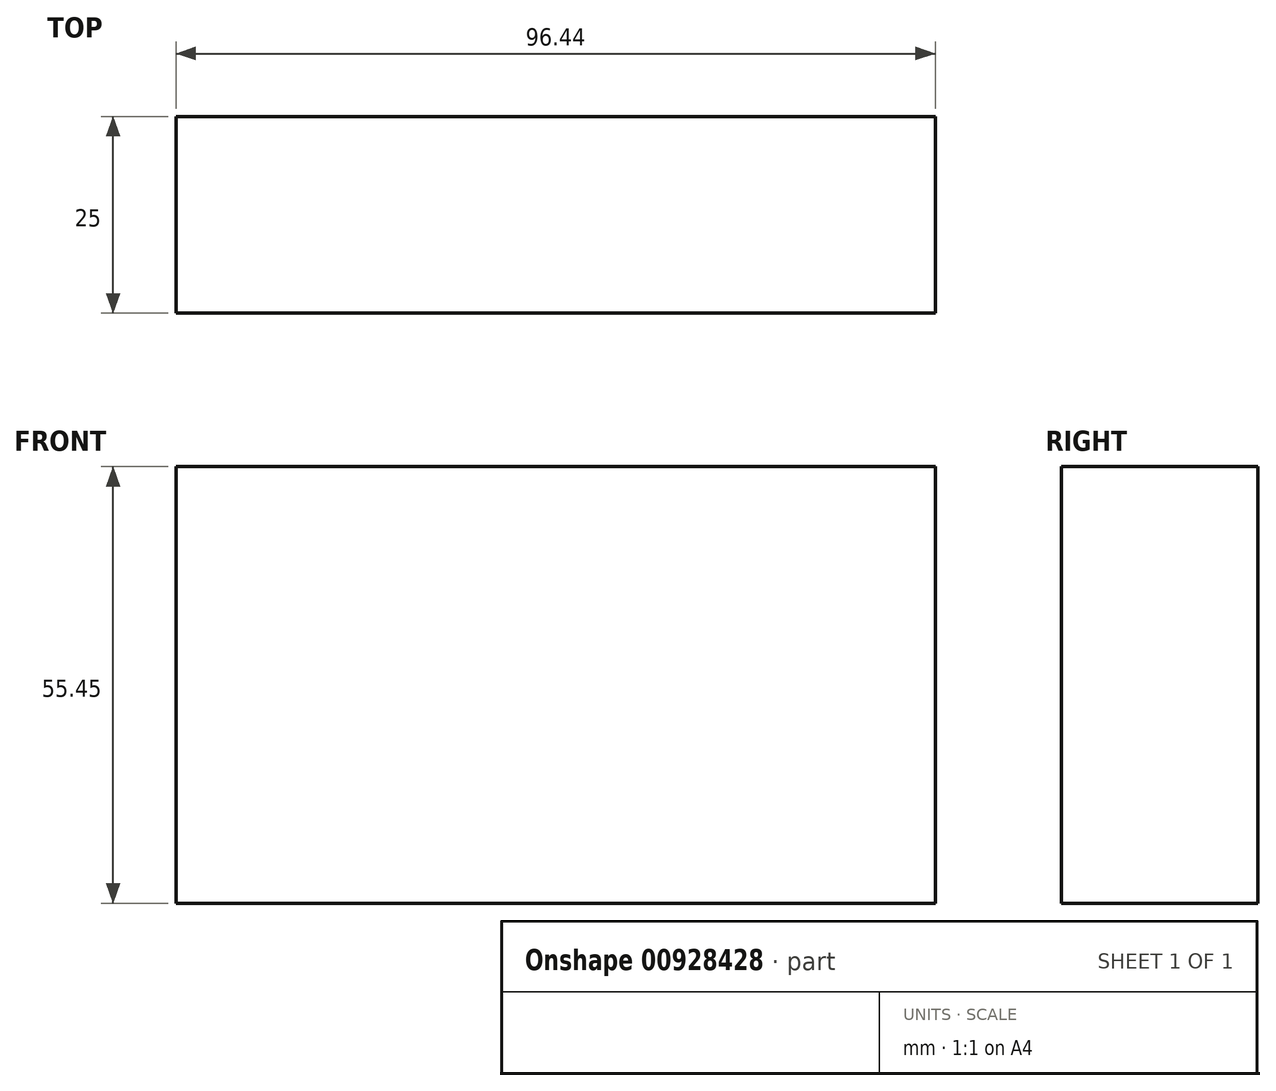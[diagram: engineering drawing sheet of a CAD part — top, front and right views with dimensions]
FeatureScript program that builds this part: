
annotation { "Feature Type Name" : "Feature", "Feature Type Description" : "" }
export const myFeature = defineFeature(function(context is Context, id is Id, definition is map)
    precondition{}
    {
        {
            var Q0;
            Q0=qCreatedBy(makeId("Front.planeOp"),FACE);
            var sketch = newSketch(context, id + "F0", { "sketchPlane" : qUnion([Q0])});
            skLineSegment(sketch, "E0.bottom", {"start": v(-73.79, 72.95) * mm, "end": v(22.65, 72.95) * mm});
            skLineSegment(sketch, "E0.top", {"start": v(-73.79, 17.5) * mm, "end": v(22.65, 17.5) * mm});
            skLineSegment(sketch, "E0.left", {"start": v(-73.79, 72.95) * mm, "end": v(-73.79, 17.5) * mm});
            skLineSegment(sketch, "E0.right", {"start": v(22.65, 72.95) * mm, "end": v(22.65, 17.5) * mm});
            skSolve(sketch);
        }
        {
            var Q0;
            Q0 = qSketchRegion(id + "F0", true);
            extrude(context, id + "F1", {"entities" : qUnion([Q0]), "depth" : 25 * mm, "offsetDistance" : 25 * mm});
        }
    });
